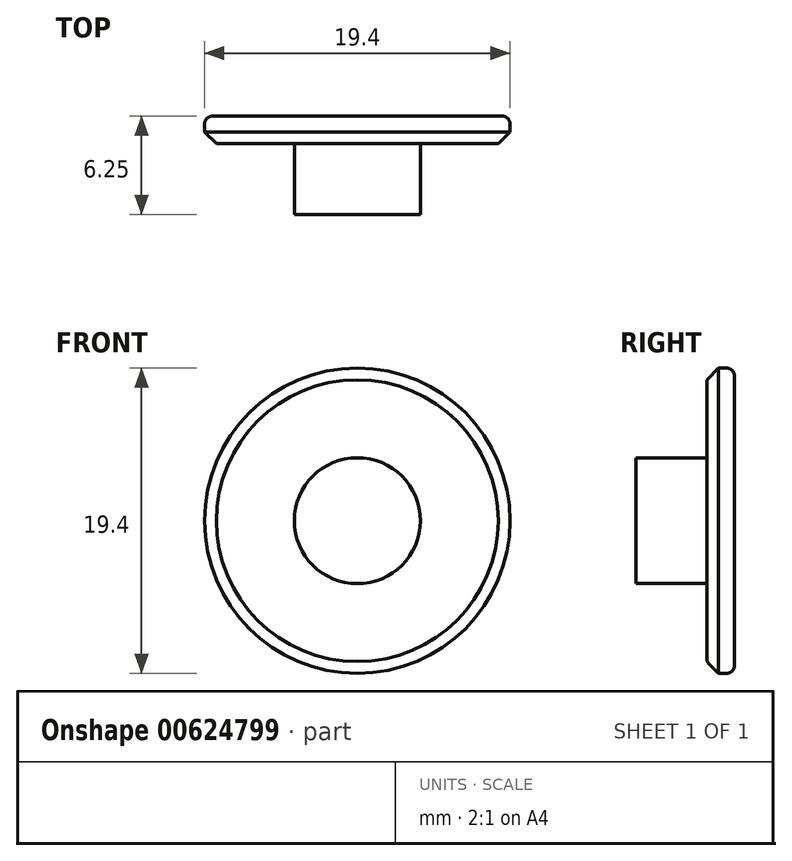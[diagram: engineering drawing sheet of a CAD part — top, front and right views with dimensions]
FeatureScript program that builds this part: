
annotation { "Feature Type Name" : "Feature", "Feature Type Description" : "" }
export const myFeature = defineFeature(function(context is Context, id is Id, definition is map)
    precondition{}
    {
        {
            var Q0;
            Q0=qCreatedBy(makeId("Front.planeOp"),FACE);
            var sketch = newSketch(context, id + "F0", { "sketchPlane" : qUnion([Q0])});
            skCircle(sketch, "E0", {"center": v(0, 0) * mm, "radius": 9.7 * mm});
            skCircle(sketch, "E1", {"center": v(0, 0) * mm, "radius": 4 * mm});
            skSolve(sketch);
        }
        {
            var Q0;
            Q0=makeQuery(id+"F0.imprint","IMPRINT",FACE,{"disambiguationData":[TD([[makeQuery(id+"F0.imprint","IMPRINT",EDGE,{"derivedFrom":sQuery(id+"F0.wireOp",EDGE,"E1")}),1.0]])]});
            extrude(context, id + "F1", {"entities" : qUnion([Q0]), "depth" : 6.25 * mm, "offsetDistance" : 25 * mm});
        }
        {
            var Q0;
            Q0=makeQuery(id+"F0.imprint","IMPRINT",FACE,{"disambiguationData":[TD([[makeQuery(id+"F0.imprint","IMPRINT",EDGE,{"derivedFrom":sQuery(id+"F0.wireOp",EDGE,"E0")}),1.0]])]});
            extrude(context, id + "F2", {"entities" : qUnion([Q0]), "operationType" : NewBodyOperationType.ADD, "depth" : 1.75 * mm, "offsetDistance" : 25 * mm});
        }
        {
            var Q0;
            Q0=makeQuery(id+"F2.opExtrude","CAP_EDGE",EDGE,{"disambiguationData":[OSD([sQuery(id+"F0.wireOp",EDGE,"E0")])],"isStart":false});
            chamfer(context, id + "F3", {"entities" : qUnion([Q0]), "width" : .75 * mm, "tangentPropagation" : true});
        }
        {
            var Q0;
            Q0=makeQuery(id+"F2.opExtrude","CAP_EDGE",EDGE,{"disambiguationData":[OSD([sQuery(id+"F0.wireOp",EDGE,"E0")])],"isStart":true});
            fillet(context, id + "F4", {"entities" : qUnion([Q0]), "radius" : .5 * mm, "tangentPropagation" : true, "allowEdgeOverflow" : false});
        }
    });
